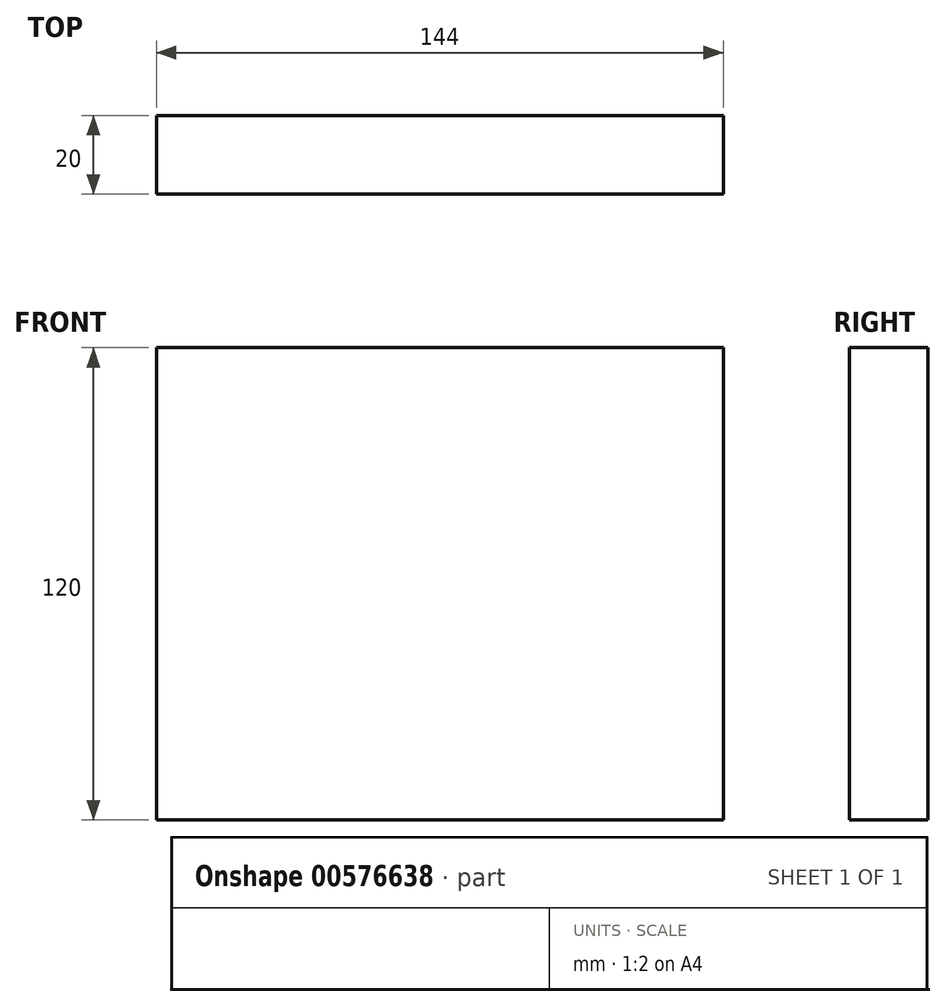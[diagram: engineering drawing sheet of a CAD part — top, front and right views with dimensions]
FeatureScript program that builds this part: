
annotation { "Feature Type Name" : "Feature", "Feature Type Description" : "" }
export const myFeature = defineFeature(function(context is Context, id is Id, definition is map)
    precondition{}
    {
        {
            var Q0;
            Q0=qCreatedBy(makeId("Front.planeOp"),FACE);
            var sketch = newSketch(context, id + "F0", { "sketchPlane" : qUnion([Q0])});
            skLineSegment(sketch, "E0.bottom", {"start": v(-72, -60) * mm, "end": v(72, -60) * mm});
            skLineSegment(sketch, "E0.top", {"start": v(-72, 60) * mm, "end": v(72, 60) * mm});
            skLineSegment(sketch, "E0.left", {"start": v(-72, -60) * mm, "end": v(-72, 60) * mm});
            skLineSegment(sketch, "E0.right", {"start": v(72, -60) * mm, "end": v(72, 60) * mm});
            skPoint(sketch, "E0.middle", {"position": v(0, 0) * mm});
            skSolve(sketch);
        }
        {
            var Q0;
            Q0 = qSketchRegion(id + "F0", true);
            extrude(context, id + "F1", {"entities" : qUnion([Q0]), "depth" : 20 * mm, "offsetDistance" : 25 * mm});
        }
    });
